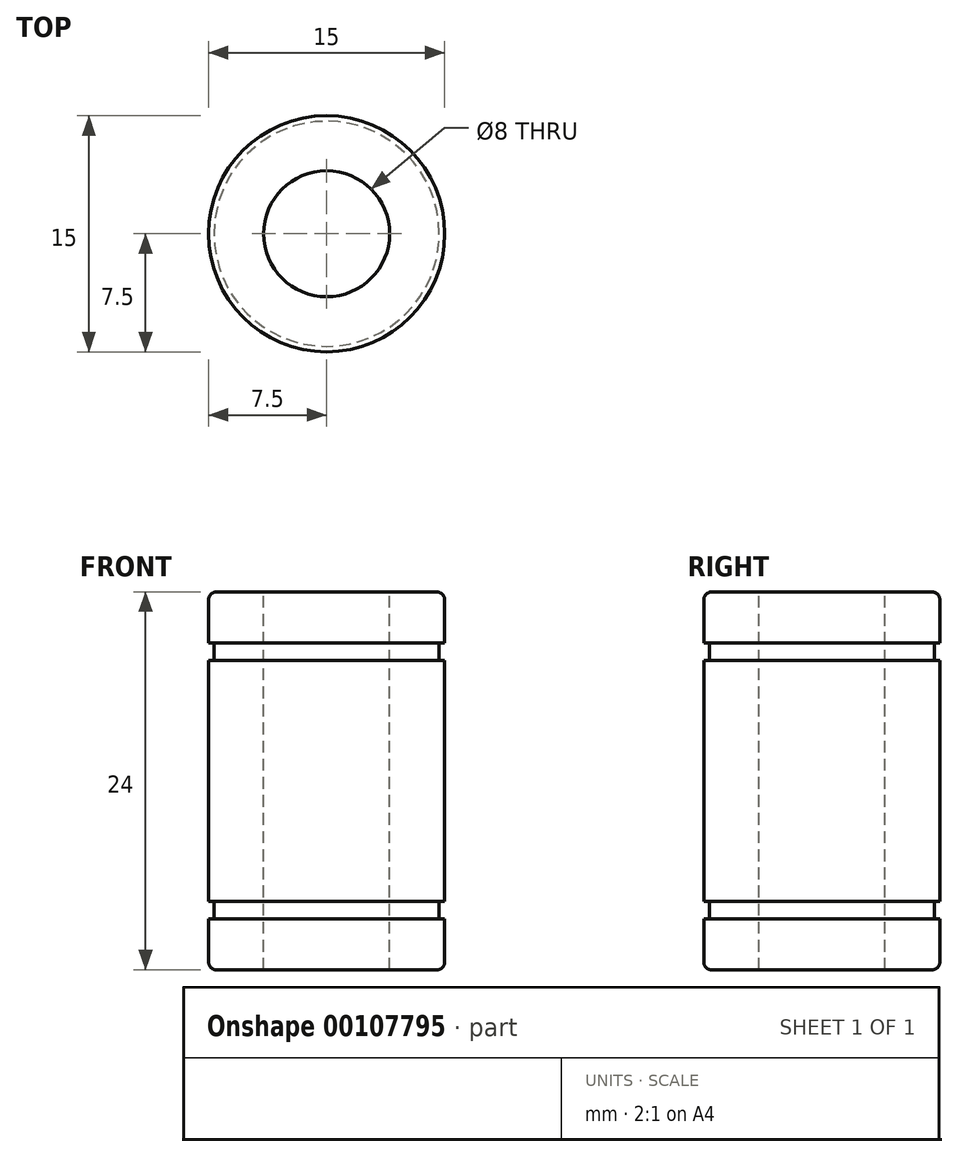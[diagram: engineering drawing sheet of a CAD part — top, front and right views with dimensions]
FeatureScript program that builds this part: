
annotation { "Feature Type Name" : "Feature", "Feature Type Description" : "" }
export const myFeature = defineFeature(function(context is Context, id is Id, definition is map)
    precondition{}
    {
        {
            var Q0;
            Q0=qCreatedBy(makeId("Front.planeOp"),FACE);
            var sketch = newSketch(context, id + "F0", { "sketchPlane" : qUnion([Q0])});
            skLineSegment(sketch, "E0", {"start": v(0, 0) * mm, "end": v(0, 24) * mm});
            skLineSegment(sketch, "E1", {"start": v(0, 24) * mm, "end": v(-7.5, 24) * mm});
            skLineSegment(sketch, "E2", {"start": v(-7.5, 24) * mm, "end": v(-7.5, 20.75) * mm});
            skLineSegment(sketch, "E3", {"start": v(-7.5, 20.75) * mm, "end": v(-7.15, 20.75) * mm});
            skLineSegment(sketch, "E4", {"start": v(-7.15, 20.75) * mm, "end": v(-7.15, 19.65) * mm});
            skLineSegment(sketch, "E5", {"start": v(-7.15, 19.65) * mm, "end": v(-7.5, 19.65) * mm});
            skLineSegment(sketch, "E6", {"start": v(-7.5, 3.25) * mm, "end": v(-7.15, 3.25) * mm});
            skLineSegment(sketch, "E7", {"start": v(-7.15, 4.35) * mm, "end": v(-7.15, 3.25) * mm});
            skLineSegment(sketch, "E8", {"start": v(-7.15, 4.35) * mm, "end": v(-7.5, 4.35) * mm});
            skLineSegment(sketch, "E9", {"start": v(-7.5, 0) * mm, "end": v(0, 0) * mm});
            skLineSegment(sketch, "E10", {"start": v(-7.5, 3.25) * mm, "end": v(-7.5, 0) * mm});
            skLineSegment(sketch, "E11", {"start": v(-7.5, 19.65) * mm, "end": v(-7.5, 4.35) * mm});
            skSolve(sketch);
        }
        {
            var Q0;
            Q0=makeQuery(id+"F0.imprint","IMPRINT",FACE,{"disambiguationData":[TD([[makeQuery(id+"F0.imprint","IMPRINT",EDGE,{"derivedFrom":sQuery(id+"F0.wireOp",EDGE,"E0")}),1.0]])]});
            var Q1;
            Q1=sQuery(id+"F0.wireOp",EDGE,"E0");
            revolve(context, id + "F1", {"entities" : qUnion([Q0]), "axis" : qUnion([Q1]), "revolveType" : RevolveType.FULL});
        }
        {
            var Q0;
            Q0=makeQuery(id+"F1.opRevolve","SWEPT_FACE",FACE,{"disambiguationData":[OSD([sQuery(id+"F0.wireOp",EDGE,"E1")])]});
            var sketch = newSketch(context, id + "F2", { "sketchPlane" : qUnion([Q0])});
            skCircle(sketch, "E12", {"center": v(0, 0) * mm, "radius": 4 * mm});
            skSolve(sketch);
        }
        {
            var Q0;
            Q0 = qSketchRegion(id + "F2", true);
            extrude(context, id + "F3", {"entities" : qUnion([Q0]), "operationType" : NewBodyOperationType.REMOVE, "oppositeDirection" : true, "depth" : 25 * mm});
        }
        {
            var Q0;
            Q0=makeQuery(id+"F1.opRevolve","SWEPT_EDGE",EDGE,{"disambiguationData":[OSD([sQuery(id+"F0.wireOp",EDGE,"E9"),sQuery(id+"F0.wireOp",EDGE,"E10")])]});
            var Q1;
            Q1=makeQuery(id+"F1.opRevolve","SWEPT_EDGE",EDGE,{"disambiguationData":[OSD([sQuery(id+"F0.wireOp",EDGE,"E1"),sQuery(id+"F0.wireOp",EDGE,"E2")])]});
            fillet(context, id + "F4", {"entities" : qUnion([Q0, Q1]), "radius" : .5 * mm, "tangentPropagation" : true, "allowEdgeOverflow" : false});
        }
    });
